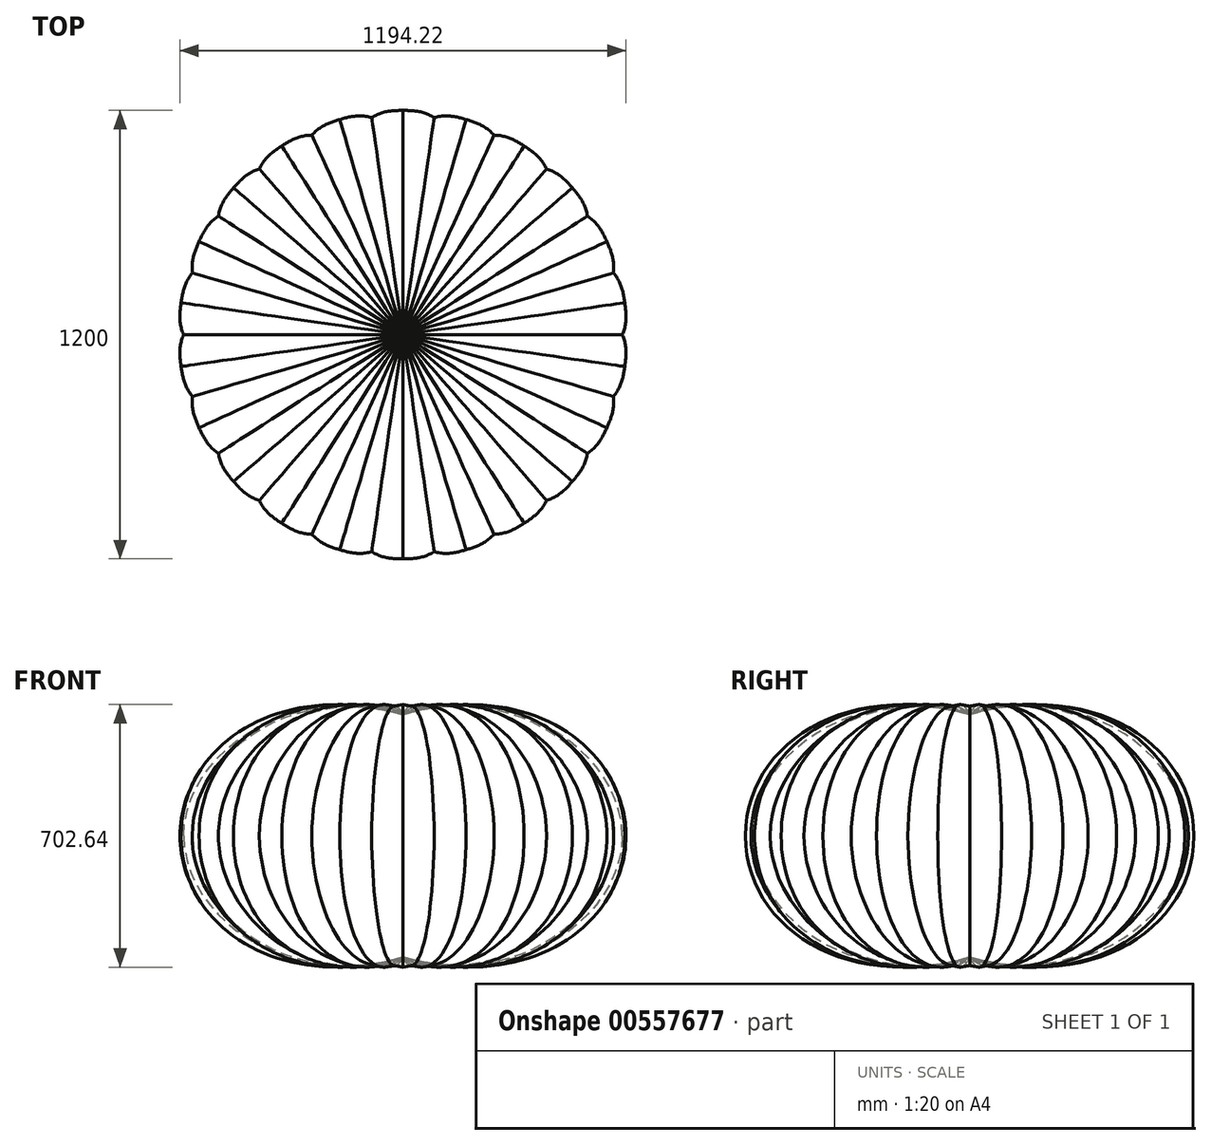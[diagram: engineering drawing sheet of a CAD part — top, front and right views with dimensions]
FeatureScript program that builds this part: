
annotation { "Feature Type Name" : "Feature", "Feature Type Description" : "" }
export const myFeature = defineFeature(function(context is Context, id is Id, definition is map)
    precondition{}
    {
        {
            var Q0;
            Q0=qCreatedBy(makeId("Right.planeOp"),FACE);
            var sketch = newSketch(context, id + "F0", { "sketchPlane" : qUnion([Q0])});
            skFitSpline(sketch, "E0", {"points": [v(0, 325) * mm, v(-600, 0) * mm], "startDerivative": vector(-975, 281.79) * mm, "endDerivative": vector(0, -750) * mm});
            skLineSegment(sketch, "E1", {"start": v(0, 0) * mm, "end": v(-600, 0) * mm});
            skLineSegment(sketch, "E2", {"start": v(0, 0) * mm, "end": v(0, 325) * mm});
            skSolve(sketch);
        }
        {
            var Q0;
            Q0=qCreatedBy(makeId("Top.planeOp"),FACE);
            var sketch = newSketch(context, id + "F1", { "sketchPlane" : qUnion([Q0])});
            skFitSpline(sketch, "E3", {"points": [v(0, -600) * mm, v(85, -580) * mm], "startDerivative": vector(84.6, 0) * mm, "endDerivative": vector(85.46, 56.23) * mm});
            skSolve(sketch);
        }
        {
            var Q0;
            Q0=sQuery(id+"F0.wireOp",VERTEX,"E0.start");
            var Q1;
            Q1=sQuery(id+"F0.wireOp",VERTEX,"E2.start");
            var Q2;
            Q2=sQuery(id+"F1.wireOp",VERTEX,"E3.1.internal");
            cPlane(context, id + "F2", {"entities" : qUnion([Q0, Q1, Q2]), "cplaneType" : CPlaneType.THREE_POINT, "offset" : 25 * mm, "width" : 150 * mm, "height" : 150 * mm});
        }
        {
            var Q0;
            Q0=qCreatedBy(id+"F2.planeOp",FACE);
            var sketch = newSketch(context, id + "F3", { "sketchPlane" : qUnion([Q0])});
            skLineSegment(sketch, "E4", {"start": v(0, 0) * mm, "end": v(0, 325) * mm});
            skLineSegment(sketch, "E5", {"start": v(0, 0) * mm, "end": v(-586.2, 0) * mm});
            skFitSpline(sketch, "E6", {"points": [v(0, 325) * mm, v(-586.2, 0) * mm], "startDerivative": vector(-969.95, 273.83) * mm, "endDerivative": vector(0, -623.49) * mm});
            skSolve(sketch);
        }
        {
            var Q0;
            Q0=makeQuery(id+"F0.imprint","IMPRINT",FACE,{"disambiguationData":[TD([[makeQuery(id+"F0.imprint","IMPRINT",EDGE,{"derivedFrom":sQuery(id+"F0.wireOp",EDGE,"E0")}),1.0]])]});
            var Q1;
            Q1=makeQuery(id+"F3.imprint","IMPRINT",FACE,{"disambiguationData":[TD([[makeQuery(id+"F3.imprint","IMPRINT",EDGE,{"derivedFrom":sQuery(id+"F3.wireOp",EDGE,"E4")}),1.0]])]});
            var Q2;
            Q2=sQuery(id+"F1.wireOp",EDGE,"E3");
            loft(context, id + "F4", {"addGuides" : true, "sheetProfilesArray" : [{ "sheetProfileEntities" : qUnion([Q0]) }, { "sheetProfileEntities" : qUnion([Q1]) }], "guidesArray" : [{ "guideEntities" : qUnion([Q2]), "guideDerivativeType" : LoftGuideDerivativeType.DEFAULT, "guideDerivativeMagnitude" : 1 }]});
        }
        {
            var Q0;
            Q0=makeQuery(id+"F4.opLoft","SWEPT_BODY",BODY,{"disambiguationData":[OSD([makeQuery(id+"F0.imprint","IMPRINT",FACE,{"disambiguationData":[TD([[makeQuery(id+"F0.imprint","IMPRINT",EDGE,{"derivedFrom":sQuery(id+"F0.wireOp",EDGE,"E0")}),1.0]])]}),sQuery(id+"F1.wireOp",EDGE,"E3"),makeQuery(id+"F3.imprint","IMPRINT",FACE,{"disambiguationData":[TD([[makeQuery(id+"F3.imprint","IMPRINT",EDGE,{"derivedFrom":sQuery(id+"F3.wireOp",EDGE,"E4")}),1.0]])]})])]});
            var Q1;
            Q1=makeQuery(id+"F4.opLoft","CAP_FACE",FACE,{"disambiguationData":[OSD([makeQuery(id+"F0.imprint","IMPRINT",FACE,{"disambiguationData":[TD([[makeQuery(id+"F0.imprint","IMPRINT",EDGE,{"derivedFrom":sQuery(id+"F0.wireOp",EDGE,"E0")}),1.0]])]})])],"isStart":true});
            mirror(context, id + "F5", {"operationType" : NewBodyOperationType.ADD, "entities" : qUnion([Q0]), "mirrorPlane" : qUnion([Q1])});
        }
        {
            var Q0;
            Q0=qCreatedBy(makeId("Front.planeOp"),FACE);
            var sketch = newSketch(context, id + "F6", { "sketchPlane" : qUnion([Q0])});
            skFitSpline(sketch, "E7", {"points": [v(0, 325) * mm, v(-550, 0) * mm], "startDerivative": vector(-863.16, 331.16) * mm, "endDerivative": vector(4.59, -733.15) * mm});
            skLineSegment(sketch, "E8", {"start": v(-550, 0) * mm, "end": v(0, 0) * mm});
            skLineSegment(sketch, "E9", {"start": v(0, 0) * mm, "end": v(0, 325) * mm});
            skSolve(sketch);
        }
        {
            var Q0;
            Q0=qCreatedBy(makeId("Top.planeOp"),FACE);
            var sketch = newSketch(context, id + "F7", { "sketchPlane" : qUnion([Q0])});
            skFitSpline(sketch, "E10", {"points": [v(-550, 0) * mm, v(-522.94, -90.3) * mm], "startDerivative": vector(-2.15, -92.4) * mm, "endDerivative": vector(64.45, -88.12) * mm});
            skSolve(sketch);
        }
        {
            var Q0;
            Q0=sQuery(id+"F7.wireOp",VERTEX,"E10.end");
            var Q1;
            Q1=sQuery(id+"F6.wireOp",VERTEX,"E7.0.internal");
            var Q2;
            Q2=sQuery(id+"F6.wireOp",VERTEX,"E9.start");
            cPlane(context, id + "F8", {"entities" : qUnion([Q0, Q1, Q2]), "cplaneType" : CPlaneType.THREE_POINT, "offset" : 25 * mm, "width" : 150 * mm, "height" : 150 * mm});
        }
        {
            var Q0;
            Q0=qCreatedBy(id+"F8.planeOp",FACE);
            var sketch = newSketch(context, id + "F9", { "sketchPlane" : qUnion([Q0])});
            skLineSegment(sketch, "E11", {"start": v(0, 0) * mm, "end": v(-530.68, 0) * mm});
            skLineSegment(sketch, "E12", {"start": v(0, 0) * mm, "end": v(0, 325) * mm});
            skFitSpline(sketch, "E13", {"points": [v(0, 325) * mm, v(-530.68, 0) * mm], "startDerivative": vector(-1023.4, 332.22) * mm, "endDerivative": vector(22.19, -788.46) * mm});
            skSolve(sketch);
        }
        {
            var Q0;
            Q0=makeQuery(id+"F4.opLoft","SWEPT_BODY",BODY,{"disambiguationData":[OSD([makeQuery(id+"F0.imprint","IMPRINT",FACE,{"disambiguationData":[TD([[makeQuery(id+"F0.imprint","IMPRINT",EDGE,{"derivedFrom":sQuery(id+"F0.wireOp",EDGE,"E0")}),1.0]])]}),sQuery(id+"F1.wireOp",EDGE,"E3"),makeQuery(id+"F3.imprint","IMPRINT",FACE,{"disambiguationData":[TD([[makeQuery(id+"F3.imprint","IMPRINT",EDGE,{"derivedFrom":sQuery(id+"F3.wireOp",EDGE,"E4")}),1.0]])]})])]});
            var Q1;
            {var subQ0=makeQuery(id+"F4.opLoft","CAP_EDGE",EDGE,{"disambiguationData":[OSD([sQuery(id+"F0.wireOp",EDGE,"E2"),sQuery(id+"F3.wireOp",EDGE,"E4")])],"isStart":false});Q1=makeQuery(id+"F5.boolean.opBoolean","MERGE",EDGE,{"derivedFrom":[subQ0,makeQuery(id+"F5.opPattern","COPY",EDGE,{"derivedFrom":subQ0,"instanceName":"1"})]});}
            circularPattern(context, id + "F10", {"operationType" : NewBodyOperationType.ADD, "entities" : qUnion([Q0]), "axis" : qUnion([Q1]), "angle" : 360 * degree, "instanceCount" : 22, "equalSpace" : true});
        }
        {
            var Q0;
            Q0=makeQuery(id+"F4.opLoft","SWEPT_BODY",BODY,{"disambiguationData":[OSD([makeQuery(id+"F0.imprint","IMPRINT",FACE,{"disambiguationData":[TD([[makeQuery(id+"F0.imprint","IMPRINT",EDGE,{"derivedFrom":sQuery(id+"F0.wireOp",EDGE,"E0")}),1.0]])]}),sQuery(id+"F1.wireOp",EDGE,"E3"),makeQuery(id+"F3.imprint","IMPRINT",FACE,{"disambiguationData":[TD([[makeQuery(id+"F3.imprint","IMPRINT",EDGE,{"derivedFrom":sQuery(id+"F3.wireOp",EDGE,"E4")}),1.0]])]})])]});
            var Q1;
            {var subQ0=makeQuery(id+"F4.opLoft","SWEPT_FACE",FACE,{"disambiguationData":[OSD([sQuery(id+"F0.wireOp",EDGE,"E1"),sQuery(id+"F0.wireOp",EDGE,"E2"),sQuery(id+"F1.wireOp",EDGE,"E3"),sQuery(id+"F3.wireOp",EDGE,"E4"),sQuery(id+"F3.wireOp",EDGE,"E5"),sQuery(id+"F3.wireOp",EDGE,"E6")])]});var subQ1=makeQuery(id+"F5.boolean.opBoolean","MERGE",FACE,{"derivedFrom":[subQ0,makeQuery(id+"F5.opPattern","COPY",FACE,{"derivedFrom":subQ0,"instanceName":"1"})]});Q1=makeQuery(id+"F10.boolean.opBoolean","MERGE",FACE,{"derivedFrom":[subQ1,makeQuery(id+"F10.opPattern","COPY",FACE,{"derivedFrom":subQ1,"instanceName":"1"}),makeQuery(id+"F10.opPattern","COPY",FACE,{"derivedFrom":subQ1,"instanceName":"2"}),makeQuery(id+"F10.opPattern","COPY",FACE,{"derivedFrom":subQ1,"instanceName":"3"}),makeQuery(id+"F10.opPattern","COPY",FACE,{"derivedFrom":subQ1,"instanceName":"4"}),makeQuery(id+"F10.opPattern","COPY",FACE,{"derivedFrom":subQ1,"instanceName":"5"}),makeQuery(id+"F10.opPattern","COPY",FACE,{"derivedFrom":subQ1,"instanceName":"6"}),makeQuery(id+"F10.opPattern","COPY",FACE,{"derivedFrom":subQ1,"instanceName":"7"}),makeQuery(id+"F10.opPattern","COPY",FACE,{"derivedFrom":subQ1,"instanceName":"8"}),makeQuery(id+"F10.opPattern","COPY",FACE,{"derivedFrom":subQ1,"instanceName":"9"}),makeQuery(id+"F10.opPattern","COPY",FACE,{"derivedFrom":subQ1,"instanceName":"10"}),makeQuery(id+"F10.opPattern","COPY",FACE,{"derivedFrom":subQ1,"instanceName":"11"}),makeQuery(id+"F10.opPattern","COPY",FACE,{"derivedFrom":subQ1,"instanceName":"12"}),makeQuery(id+"F10.opPattern","COPY",FACE,{"derivedFrom":subQ1,"instanceName":"13"}),makeQuery(id+"F10.opPattern","COPY",FACE,{"derivedFrom":subQ1,"instanceName":"14"}),makeQuery(id+"F10.opPattern","COPY",FACE,{"derivedFrom":subQ1,"instanceName":"15"}),makeQuery(id+"F10.opPattern","COPY",FACE,{"derivedFrom":subQ1,"instanceName":"16"}),makeQuery(id+"F10.opPattern","COPY",FACE,{"derivedFrom":subQ1,"instanceName":"17"}),makeQuery(id+"F10.opPattern","COPY",FACE,{"derivedFrom":subQ1,"instanceName":"18"}),makeQuery(id+"F10.opPattern","COPY",FACE,{"derivedFrom":subQ1,"instanceName":"19"}),makeQuery(id+"F10.opPattern","COPY",FACE,{"derivedFrom":subQ1,"instanceName":"20"}),makeQuery(id+"F10.opPattern","COPY",FACE,{"derivedFrom":subQ1,"instanceName":"21"})]});}
            mirror(context, id + "F11", {"operationType" : NewBodyOperationType.ADD, "entities" : qUnion([Q0]), "mirrorPlane" : qUnion([Q1])});
        }
    });
